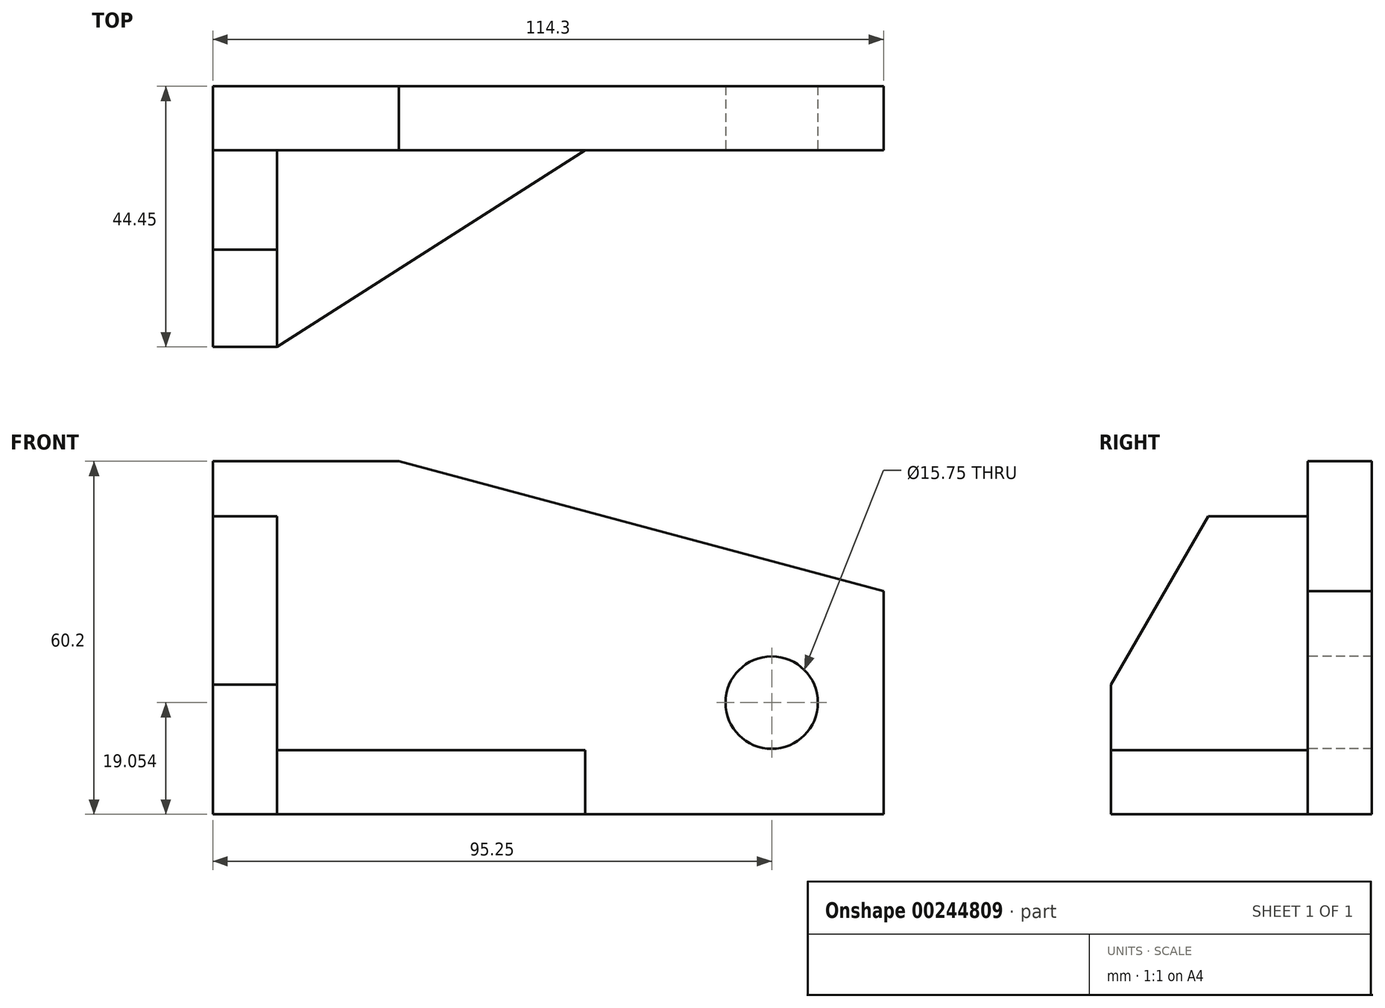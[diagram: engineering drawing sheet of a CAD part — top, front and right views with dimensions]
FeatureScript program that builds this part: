
annotation { "Feature Type Name" : "Feature", "Feature Type Description" : "" }
export const myFeature = defineFeature(function(context is Context, id is Id, definition is map)
    precondition{}
    {
        {
            var Q0;
            Q0=qCreatedBy(makeId("Front.planeOp"),FACE);
            var sketch = newSketch(context, id + "F0", { "sketchPlane" : qUnion([Q0])});
            skLineSegment(sketch, "E0.top", {"start": v(57.15, -31.4) * mm, "end": v(-57.15, -31.4) * mm});
            skLineSegment(sketch, "E0.right", {"start": v(-57.15, 28.8) * mm, "end": v(-57.15, -31.4) * mm});
            skLineSegment(sketch, "E1", {"start": v(-57.15, 28.8) * mm, "end": v(-25.4, 28.8) * mm});
            skLineSegment(sketch, "E2", {"start": v(-25.4, 28.8) * mm, "end": v(57.15, 6.67) * mm});
            skLineSegment(sketch, "E3", {"start": v(-25.4, 28.8) * mm, "end": v(57.15, 28.8) * mm, "construction": true});
            skLineSegment(sketch, "E4", {"start": v(57.15, 6.67) * mm, "end": v(57.15, -31.4) * mm});
            skSolve(sketch);
        }
        {
            var Q0;
            Q0=makeQuery(id+"F0.imprint","IMPRINT",FACE,{"disambiguationData":[TD([[makeQuery(id+"F0.imprint","IMPRINT",EDGE,{"derivedFrom":sQuery(id+"F0.wireOp",EDGE,"E0.top")}),-1.0]])]});
            extrude(context, id + "F1", {"entities" : qUnion([Q0]), "depth" : 10.92 * mm});
        }
        {
            var Q0;
            Q0=makeQuery(id+"F1.opExtrude","CAP_FACE",FACE,{"disambiguationData":[OSD([sQuery(id+"F0.wireOp",EDGE,"E0.top"),sQuery(id+"F0.wireOp",EDGE,"E0.right"),sQuery(id+"F0.wireOp",EDGE,"E1"),sQuery(id+"F0.wireOp",EDGE,"E2"),sQuery(id+"F0.wireOp",EDGE,"E4")])],"isStart":false});
            var sketch = newSketch(context, id + "F2", { "sketchPlane" : qUnion([Q0])});
            skLineSegment(sketch, "E5", {"start": v(57.15, -31.4) * mm, "end": v(38.1, -31.4) * mm, "construction": true});
            skLineSegment(sketch, "E6", {"start": v(38.1, -12.36) * mm, "end": v(38.1, -31.4) * mm, "construction": true});
            skCircle(sketch, "E7", {"center": v(38.1, -12.36) * mm, "radius": 7.87 * mm});
            skSolve(sketch);
        }
        {
            var Q0;
            Q0 = qSketchRegion(id + "F2", true);
            extrude(context, id + "F3", {"entities" : qUnion([Q0]), "operationType" : NewBodyOperationType.REMOVE, "endBound" : BoundingType.THROUGH_ALL, "oppositeDirection" : true, "depth" : 25.4 * mm});
        }
        {
            var Q0;
            Q0=makeQuery(id+"F1.opExtrude","SWEPT_FACE",FACE,{"disambiguationData":[OSD([sQuery(id+"F0.wireOp",EDGE,"E0.top")])]});
            var sketch = newSketch(context, id + "F4", { "sketchPlane" : qUnion([Q0])});
            skLineSegment(sketch, "E8", {"start": v(-57.15, 10.92) * mm, "end": v(-46.23, 10.92) * mm, "construction": true});
            skLineSegment(sketch, "E9", {"start": v(-46.23, 10.92) * mm, "end": v(6.35, 10.92) * mm});
            skLineSegment(sketch, "E10", {"start": v(-46.23, 10.92) * mm, "end": v(-46.23, 44.45) * mm});
            skLineSegment(sketch, "E11", {"start": v(-46.23, 44.45) * mm, "end": v(6.35, 10.92) * mm});
            skSolve(sketch);
        }
        {
            var Q0;
            Q0 = qSketchRegion(id + "F4", true);
            extrude(context, id + "F5", {"entities" : qUnion([Q0]), "oppositeDirection" : true, "depth" : 10.92 * mm});
        }
        {
            var Q0;
            Q0=makeQuery(id+"F1.opExtrude","SWEPT_FACE",FACE,{"disambiguationData":[OSD([sQuery(id+"F0.wireOp",EDGE,"E0.right")])]});
            var sketch = newSketch(context, id + "F6", { "sketchPlane" : qUnion([Q0])});
            skLineSegment(sketch, "E12", {"start": v(10.92, -31.4) * mm, "end": v(44.45, -31.4) * mm});
            skLineSegment(sketch, "E13", {"start": v(44.45, -31.4) * mm, "end": v(44.45, -9.3) * mm});
            skLineSegment(sketch, "E14", {"start": v(44.45, -9.3) * mm, "end": v(44.45, 19.4) * mm, "construction": true});
            skLineSegment(sketch, "E15", {"start": v(44.45, -9.3) * mm, "end": v(27.88, 19.4) * mm});
            skLineSegment(sketch, "E16", {"start": v(27.88, 19.4) * mm, "end": v(10.92, 19.4) * mm});
            skSolve(sketch);
        }
        {
            var Q0;
            {var subQ1=sQuery(id+"F6.wireOp",EDGE,"E12");Q0=makeQuery(id+"F6.imprint","IMPRINT",FACE,{"disambiguationData":[TD([[makeQuery(id+"F6.imprint","IMPRINT",EDGE,{"derivedFrom":subQ1}),1.0]])]});}
            extrude(context, id + "F7", {"entities" : qUnion([Q0]), "oppositeDirection" : true, "depth" : 10.92 * mm});
        }
    });
